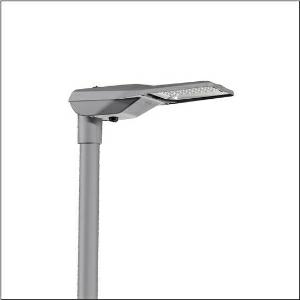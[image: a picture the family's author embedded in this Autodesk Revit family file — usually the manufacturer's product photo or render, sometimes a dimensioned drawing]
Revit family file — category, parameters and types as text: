
# Revit family: streetlight_sl_21_iq_mini___st1_0a_5xe2d31y08gb_99d1
name_source: partatom
category: Lighting Fixtures
units: mm (PartAtom-declared; Revit-internal decimal feet)

## family parameters
Cut with Voids When Loaded = No
Host = Face
Light Source = No
Part Type = Normal
Room Calculation Point = No
Round Connector Dimension = Use Diameter
Shared = No

## types (1)
- --- (1 x LED, 5990 lm, 39.8 W, 3000K)
    Apparent Load = 40 VA
    CIE Flux Codes = 37 72 97 100 100
    Color Rendering = 70
    Color Temperature = 3000K
    Default Elevation = 1800 mm
    Description = Streetlight SL 21 iQ mini, mast luminaire, primary light control with lens, of PMMA, primary optical cover: cover, of toughened safety glass, transparent, light distribution: ST1.0a, light emission: direct distribution, primary light characteristic: asymmetric, installation type: post-top, side-entry, LED, High Power LED, rated luminous flux: 5.990lm, luminous efficacy: 151lm/W, light colour: 730, colour temperature: 3000K, control gear: iQ-Street Remote, D4i with power reduction, control: pre-setting: logarithmic dimming characteristic, Street-Remote, Auto-Match, Temp-Guard, Lumen-Switch, Night-Set, Smart-Wire, Light-Fading, Desk-Remote (wireless, voltage-free reading and setting of iQ features in the workshop via application-optimized NFC function/RFID function), optimised constant luminous flux control (CLO 2.0), mains connection: 220..240V, AC, 50/60Hz, start of lifetime: 40W, end of service life: 41W, reduction: 18W, luminaire housing, of diecast aluminium, powder-coated, Siteco® metallic grey (DB 702S), corrosivity category C5 mid according to DIN EN ISO 12944, please order mast flange separately, inclination adjustable: 0°, 5°, 10°, 15°, sealing non-destructively replaceable, multi-level sealing system, length: 628mm, width: 235mm, height: 110mm, mast flange for spigot size: 42mm (side-entry): 5XC10008XM4, 60/48mm (side-entry/post-top): 5XC10108XM2, 76/60mm (side-entry/post-top): 5XC10108XM1, mounting height: 4..8m, Smart Interface below and above, protection rating (complete): IP66, insulation class (complete): insulation class II (safety insulation), certification: CE, ENEC, ENEC+, VDE, impact resistance: IK10, permissible operating ambient temperature for outdoor applications: -40..+50°C, standard-compliant lighting for roads and squares, packaging unit: 1 piece

Light Distribution: ST1.0a
    Height = 110 mm
    Lamp = 1 x LED
    Lamp Light Flux = 5990 lm
    Lamp Power = 39.8 W
    Lamp count = 1
    Length = 625 mm
    Luminous efficacy = 151 lm/W
    Manufacturer = Siteco
    ModVariant = No
    Model = 5XE2D31Y08GB
    Number of Poles = 1
    OnlyDefault = Yes
    Power Factor = 1
    Product Name = Streetlight SL 21 iQ mini | ST1.0a
    Product group = mast luminaire | pylon top
    ProductGroupID = 6100
    Protection Class = Protection class II
    Protection Degree = IP 66
    RLX_Detail_Level = 1
    RLX_Emergency_Light_Flux = 0 lm
    RLX_Emergency_Type = 0
    RLX_Emergency_Type_DB = No
    RlxData = <blob elided: 92817 chars, md5=48c5925a>
    Socket = socket
    Standby Power = 0 W
    System Light Flux = 5990 lm
    System Power = 40 W
    Type Comments = factory setting: luminous flux: 100 % | dim-lin: 254 | 800 mA
    Type Image = l_1003514.jpg
    URL = http://relux.com
    VarID = @adj_136391
    Voltage = 0 V
    Weight = 0.00 kg
    Width = 234 mm

## geometry (parser evidence)
native form markers: Blend x4, Sweep x11
no freeform markers — native parametric forms only
